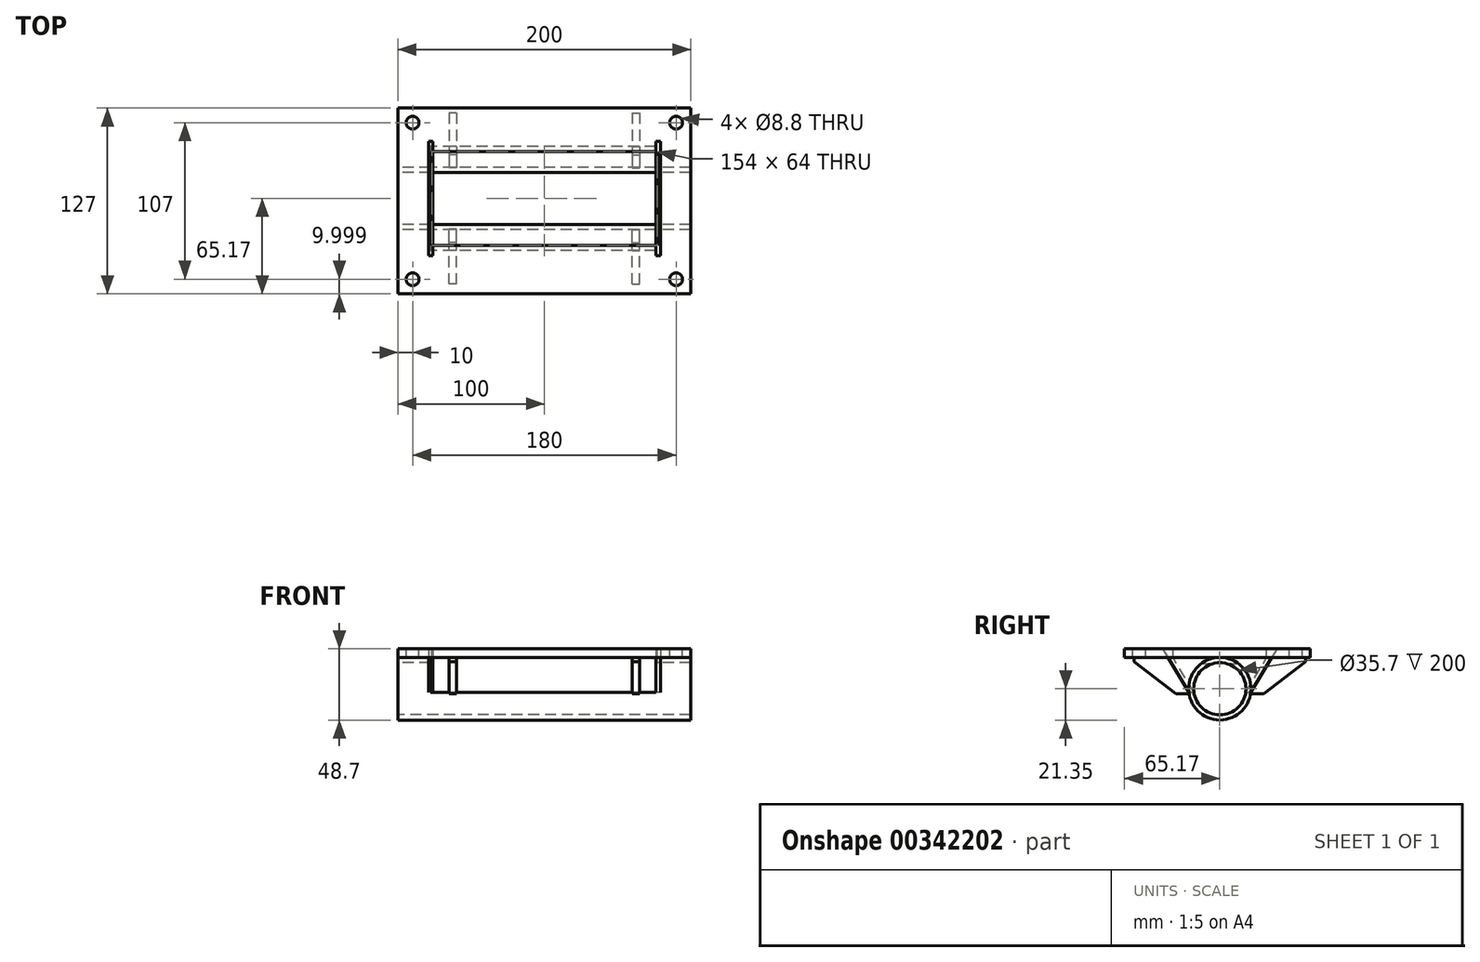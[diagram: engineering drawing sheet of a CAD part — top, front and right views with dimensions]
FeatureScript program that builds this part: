
annotation { "Feature Type Name" : "Feature", "Feature Type Description" : "" }
export const myFeature = defineFeature(function(context is Context, id is Id, definition is map)
    precondition{}
    {
        {
            var Q0;
            Q0=qCreatedBy(makeId("Right.planeOp"),FACE);
            var sketch = newSketch(context, id + "F0", { "sketchPlane" : qUnion([Q0])});
            skCircle(sketch, "E0", {"center": v(0, 0) * mm, "radius": 17.85 * mm});
            skCircle(sketch, "E1", {"center": v(0, 0) * mm, "radius": 21.35 * mm});
            skSolve(sketch);
        }
        {
            var Q0;
            Q0 = qSketchRegion(id + "F0", true);
            extrude(context, id + "F1", {"entities" : qUnion([Q0]), "endBound" : BoundingType.SYMMETRIC, "depth" : 200 * mm});
        }
        {
            var Q0;
            Q0=qCreatedBy(makeId("Front.planeOp"),FACE);
            var sketch = newSketch(context, id + "F2", { "sketchPlane" : qUnion([Q0])});
            skLineSegment(sketch, "E2.bottom", {"start": v(-77.78, 58.63) * mm, "end": v(76.22, 58.63) * mm});
            skLineSegment(sketch, "E2.top", {"start": v(-77.78, -2.45) * mm, "end": v(76.22, -2.45) * mm});
            skLineSegment(sketch, "E2.left", {"start": v(-77.78, 58.63) * mm, "end": v(-77.78, -2.45) * mm});
            skLineSegment(sketch, "E2.right", {"start": v(76.22, 58.63) * mm, "end": v(76.22, -2.45) * mm});
            skLineSegment(sketch, "E3.bottom", {"start": v(0, 0) * mm, "end": v(0, 0) * mm});
            skLineSegment(sketch, "E3.top", {"start": v(0, 146.95) * mm, "end": v(0, 146.95) * mm});
            skLineSegment(sketch, "E3.left", {"start": v(0, 0) * mm, "end": v(0, 146.95) * mm, "construction": true});
            skLineSegment(sketch, "E3.right", {"start": v(0, 0) * mm, "end": v(0, 146.95) * mm, "construction": true});
            skSolve(sketch);
        }
        {
            var Q0;
            Q0 = qSketchRegion(id + "F2", true);
            extrude(context, id + "F3", {"entities" : qUnion([Q0]), "operationType" : NewBodyOperationType.REMOVE, "endBound" : BoundingType.SYMMETRIC, "oppositeDirection" : true, "depth" : 100 * mm});
        }
        {
            var Q0;
            Q0=qCreatedBy(makeId("Right.planeOp"),FACE);
            var sketch = newSketch(context, id + "F4", { "sketchPlane" : qUnion([Q0])});
            skLineSegment(sketch, "E4.bottom", {"start": v(-65.17, 27.35) * mm, "end": v(61.83, 27.35) * mm});
            skLineSegment(sketch, "E4.top", {"start": v(-65.17, 21.35) * mm, "end": v(61.83, 21.35) * mm});
            skLineSegment(sketch, "E4.left", {"start": v(-65.17, 27.35) * mm, "end": v(-65.17, 21.35) * mm});
            skLineSegment(sketch, "E4.right", {"start": v(61.83, 27.35) * mm, "end": v(61.83, 21.35) * mm});
            skLineSegment(sketch, "E5.bottom", {"start": v(0, 0) * mm, "end": v(0, 0) * mm});
            skLineSegment(sketch, "E5.top", {"start": v(0, 89.74) * mm, "end": v(0, 89.74) * mm});
            skLineSegment(sketch, "E5.left", {"start": v(0, 0) * mm, "end": v(0, 89.74) * mm, "construction": true});
            skLineSegment(sketch, "E5.right", {"start": v(0, 0) * mm, "end": v(0, 89.74) * mm, "construction": true});
            skSolve(sketch);
        }
        {
            var Q0;
            Q0 = qSketchRegion(id + "F4", true);
            extrude(context, id + "F5", {"entities" : qUnion([Q0]), "operationType" : NewBodyOperationType.ADD, "endBound" : BoundingType.SYMMETRIC, "depth" : 200 * mm});
        }
        {
            var Q0;
            Q0=makeQuery(id+"F5.opExtrude","SWEPT_FACE",FACE,{"disambiguationData":[OSD([sQuery(id+"F4.wireOp",EDGE,"E4.bottom")])]});
            var sketch = newSketch(context, id + "F6", { "sketchPlane" : qUnion([Q0])});
            skLineSegment(sketch, "E6.bottom", {"start": v(77, 32) * mm, "end": v(-77, 32) * mm});
            skLineSegment(sketch, "E6.top", {"start": v(77, -32) * mm, "end": v(-77, -32) * mm});
            skLineSegment(sketch, "E6.left", {"start": v(77, 32) * mm, "end": v(77, -32) * mm});
            skLineSegment(sketch, "E6.right", {"start": v(-77, 32) * mm, "end": v(-77, -32) * mm});
            skPoint(sketch, "E6.middle", {"position": v(0, 0) * mm});
            skSolve(sketch);
        }
        {
            var Q0;
            Q0 = qSketchRegion(id + "F6", true);
            extrude(context, id + "F7", {"entities" : qUnion([Q0]), "operationType" : NewBodyOperationType.REMOVE, "oppositeDirection" : true, "depth" : 10 * mm});
        }
        {
            var Q0;
            Q0=makeQuery(id+"F3.boolean.opBoolean","COPY",FACE,{"derivedFrom":makeQuery(id+"F3.opExtrude","SWEPT_FACE",FACE,{"disambiguationData":[OSD([sQuery(id+"F2.wireOp",EDGE,"E2.left")])]})});
            var sketch = newSketch(context, id + "F8", { "sketchPlane" : qUnion([Q0])});
            skLineSegment(sketch, "E7", {"start": v(-32, 21.35) * mm, "end": v(-17.68, -2.45) * mm});
            skLineSegment(sketch, "E8.0", {"start": v(-35.5, 21.35) * mm, "end": v(-21.18, -2.45) * mm});
            skLineSegment(sketch, "E9", {"start": v(-17.68, -2.45) * mm, "end": v(-21.2, -2.45) * mm});
            skLineSegment(sketch, "E10", {"start": v(-35.5, 21.35) * mm, "end": v(-32, 21.35) * mm});
            skLineSegment(sketch, "E11", {"start": v(0, 0) * mm, "end": v(0, 42.29) * mm, "construction": true});
            skLineSegment(sketch, "E12.MirrorCS", {"start": v(32, 21.35) * mm, "end": v(17.68, -2.45) * mm});
            skLineSegment(sketch, "E13.MirrorCS", {"start": v(35.5, 21.35) * mm, "end": v(21.18, -2.45) * mm});
            skLineSegment(sketch, "E14", {"start": v(32, 21.35) * mm, "end": v(35.5, 21.35) * mm});
            skLineSegment(sketch, "E15", {"start": v(17.68, -2.45) * mm, "end": v(21.2, -2.45) * mm});
            skSolve(sketch);
        }
        {
            var Q0;
            Q0 = qSketchRegion(id + "F8", true);
            var Q1;
            Q1=makeQuery(id+"F3.boolean.opBoolean","COPY",FACE,{"derivedFrom":makeQuery(id+"F3.opExtrude","SWEPT_FACE",FACE,{"disambiguationData":[OSD([sQuery(id+"F2.wireOp",EDGE,"E2.right")])]})});
            extrude(context, id + "F9", {"entities" : qUnion([Q0]), "endBound" : BoundingType.UP_TO_SURFACE, "endBoundEntityFace" : qUnion([Q1]), "depth" : 25 * mm});
        }
        {
            var Q0;
            Q0=makeQuery(id+"F3.boolean.opBoolean","COPY",FACE,{"derivedFrom":makeQuery(id+"F3.opExtrude","SWEPT_FACE",FACE,{"disambiguationData":[OSD([sQuery(id+"F2.wireOp",EDGE,"E2.right")])]})});
            var sketch = newSketch(context, id + "F10", { "sketchPlane" : qUnion([Q0])});
            skArc(sketch, "E16.0", {"start": v(17.68, -2.45) * mm, "mid": v(0, 17.85) * mm, "end": v(-17.68, -2.45) * mm});
            skLineSegment(sketch, "E16.1", {"start": v(-39.11, 27.35) * mm, "end": v(-21.18, -2.45) * mm});
            skLineSegment(sketch, "E16.2", {"start": v(39.11, 27.35) * mm, "end": v(21.18, -2.45) * mm});
            skLineSegment(sketch, "E16.3", {"start": v(39.11, 27.35) * mm, "end": v(-39.11, 27.35) * mm});
            skPoint(sketch, "E17.orphan", {"position": v(-35.5, 21.35) * mm});
            skPoint(sketch, "E18.orphan", {"position": v(35.5, 21.35) * mm});
            skLineSegment(sketch, "E19", {"start": v(-21.18, -2.45) * mm, "end": v(-17.68, -2.45) * mm});
            skLineSegment(sketch, "E20.trimOffspring", {"start": v(17.68, -2.45) * mm, "end": v(21.2, -2.45) * mm});
            skSolve(sketch);
        }
        {
            var Q0;
            Q0 = qSketchRegion(id + "F10", true);
            extrude(context, id + "F11", {"entities" : qUnion([Q0]), "oppositeDirection" : true, "depth" : 3 * mm});
        }
        {
            var Q0;
            Q0=makeQuery(id+"F11.opExtrude","SWEPT_BODY",BODY,{"disambiguationData":[OSD([sQuery(id+"F10.wireOp",EDGE,"E16.0"),sQuery(id+"F10.wireOp",EDGE,"E16.1"),sQuery(id+"F10.wireOp",EDGE,"E16.2"),sQuery(id+"F10.wireOp",EDGE,"E16.3"),sQuery(id+"F10.wireOp",EDGE,"E19"),sQuery(id+"F10.wireOp",EDGE,"E20.trimOffspring")])]});
            var Q1;
            Q1=qCreatedBy(makeId("Right.planeOp"),FACE);
            mirror(context, id + "F12", {"entities" : qUnion([Q0]), "mirrorPlane" : qUnion([Q1])});
        }
        {
            var Q0;
            Q0=qCreatedBy(makeId("Right.planeOp"),FACE);
            cPlane(context, id + "F13", {"entities" : qUnion([Q0]), "cplaneType" : CPlaneType.OFFSET, "offset" : 65 * mm, "width" : 150 * mm, "height" : 150 * mm});
        }
        {
            var Q0;
            Q0=qCreatedBy(id+"F13.planeOp",FACE);
            var sketch = newSketch(context, id + "F14", { "sketchPlane" : qUnion([Q0])});
            skLineSegment(sketch, "E21.0", {"start": v(-35.5, 21.35) * mm, "end": v(-21.18, -2.45) * mm});
            skArc(sketch, "E21.1", {"start": v(-21.22, -2.4) * mm, "mid": v(-21.15, -2.92) * mm, "end": v(-21.07, -3.45) * mm});
            skLineSegment(sketch, "E22.0", {"start": v(-30, -3.45) * mm, "end": v(-21.07, -3.45) * mm});
            skLineSegment(sketch, "E23.0", {"start": v(-58.5, 18.35) * mm, "end": v(-58.5, 21.35) * mm});
            skLineSegment(sketch, "E24.0", {"start": v(-58.5, 21.35) * mm, "end": v(-35.5, 21.35) * mm});
            skLineSegment(sketch, "E25", {"start": v(-58.5, 18.35) * mm, "end": v(-30, -3.45) * mm});
            skSolve(sketch);
        }
        {
            var Q0;
            Q0 = qSketchRegion(id + "F14", true);
            extrude(context, id + "F15", {"entities" : qUnion([Q0]), "oppositeDirection" : true, "depth" : 5 * mm});
        }
        {
            var Q0;
            Q0=makeQuery(id+"F15.opExtrude","SWEPT_BODY",BODY,{"disambiguationData":[OSD([sQuery(id+"F14.wireOp",EDGE,"E21.0"),sQuery(id+"F14.wireOp",EDGE,"E21.1"),sQuery(id+"F14.wireOp",EDGE,"E22.0"),sQuery(id+"F14.wireOp",EDGE,"E23.0"),sQuery(id+"F14.wireOp",EDGE,"E24.0"),sQuery(id+"F14.wireOp",EDGE,"E25")])]});
            var Q1;
            Q1=qCreatedBy(makeId("Right.planeOp"),FACE);
            mirror(context, id + "F16", {"entities" : qUnion([Q0]), "mirrorPlane" : qUnion([Q1])});
        }
        {
            var Q0;
            Q0=makeQuery(id+"F15.opExtrude","SWEPT_BODY",BODY,{"disambiguationData":[OSD([sQuery(id+"F14.wireOp",EDGE,"E21.0"),sQuery(id+"F14.wireOp",EDGE,"E21.1"),sQuery(id+"F14.wireOp",EDGE,"E22.0"),sQuery(id+"F14.wireOp",EDGE,"E23.0"),sQuery(id+"F14.wireOp",EDGE,"E24.0"),sQuery(id+"F14.wireOp",EDGE,"E25")])]});
            var Q1;
            Q1=makeQuery(id+"F16.opPattern","COPY",BODY,{"derivedFrom":makeQuery(id+"F15.opExtrude","SWEPT_BODY",BODY,{"disambiguationData":[OSD([sQuery(id+"F14.wireOp",EDGE,"E21.0"),sQuery(id+"F14.wireOp",EDGE,"E21.1"),sQuery(id+"F14.wireOp",EDGE,"E22.0"),sQuery(id+"F14.wireOp",EDGE,"E23.0"),sQuery(id+"F14.wireOp",EDGE,"E24.0"),sQuery(id+"F14.wireOp",EDGE,"E25")])]}),"instanceName":"1"});
            var Q2;
            Q2=qCreatedBy(makeId("Front.planeOp"),FACE);
            mirror(context, id + "F17", {"entities" : qUnion([Q0, Q1]), "mirrorPlane" : qUnion([Q2])});
        }
        {
            var Q0;
            Q0=makeQuery(id+"F5.opExtrude","SWEPT_FACE",FACE,{"disambiguationData":[OSD([sQuery(id+"F4.wireOp",EDGE,"E4.bottom")])]});
            var sketch = newSketch(context, id + "F18", { "sketchPlane" : qUnion([Q0])});
            skLineSegment(sketch, "E26.bottom", {"start": v(-90, 51.83) * mm, "end": v(90, 51.83) * mm});
            skLineSegment(sketch, "E26.top", {"start": v(-90, -55.17) * mm, "end": v(90, -55.17) * mm});
            skLineSegment(sketch, "E26.left", {"start": v(-90, 51.83) * mm, "end": v(-90, -55.17) * mm});
            skLineSegment(sketch, "E26.right", {"start": v(90, 51.83) * mm, "end": v(90, -55.17) * mm});
            skSolve(sketch);
        }
        {
            var Q0;
            Q0=sQuery(id+"F18.wireOp",VERTEX,"E26.left.start");
            var Q1;
            Q1=sQuery(id+"F18.wireOp",VERTEX,"E26.right.start");
            var Q2;
            Q2=sQuery(id+"F18.wireOp",VERTEX,"E26.right.end");
            var Q3;
            Q3=sQuery(id+"F18.wireOp",VERTEX,"E26.left.end");
            var Q4;
            Q4=makeQuery(id+"F5.opExtrude","SWEPT_BODY",BODY,{"disambiguationData":[OSD([sQuery(id+"F4.wireOp",EDGE,"E4.bottom"),sQuery(id+"F4.wireOp",EDGE,"E4.top"),sQuery(id+"F4.wireOp",EDGE,"E4.left"),sQuery(id+"F4.wireOp",EDGE,"E4.right")])]});
            hole(context, id + "F19", {"style" : HoleStyle.SIMPLE, "endStyle" : HoleEndStyle.THROUGH, "standardTappedOrClearance" : lookupTablePath({ "standard" : "ISO", "fit" : "Normal", "size" : "M8", "type" : "Clearance" }), "standardBlindInLast" : lookupTablePath({ "fit" : "Standard", "standard" : "ISO", "size" : "M8", "type" : "Clearance" }), "holeDiameter" : 8.8 * mm, "isTappedThrough" : true, "tappedDepth" : 12 * mm, "tapClearance" : 3, "startFromSketch" : true, "locations" : qUnion([Q0, Q1, Q2, Q3]), "scope" : qUnion([Q4])});
        }
    });
